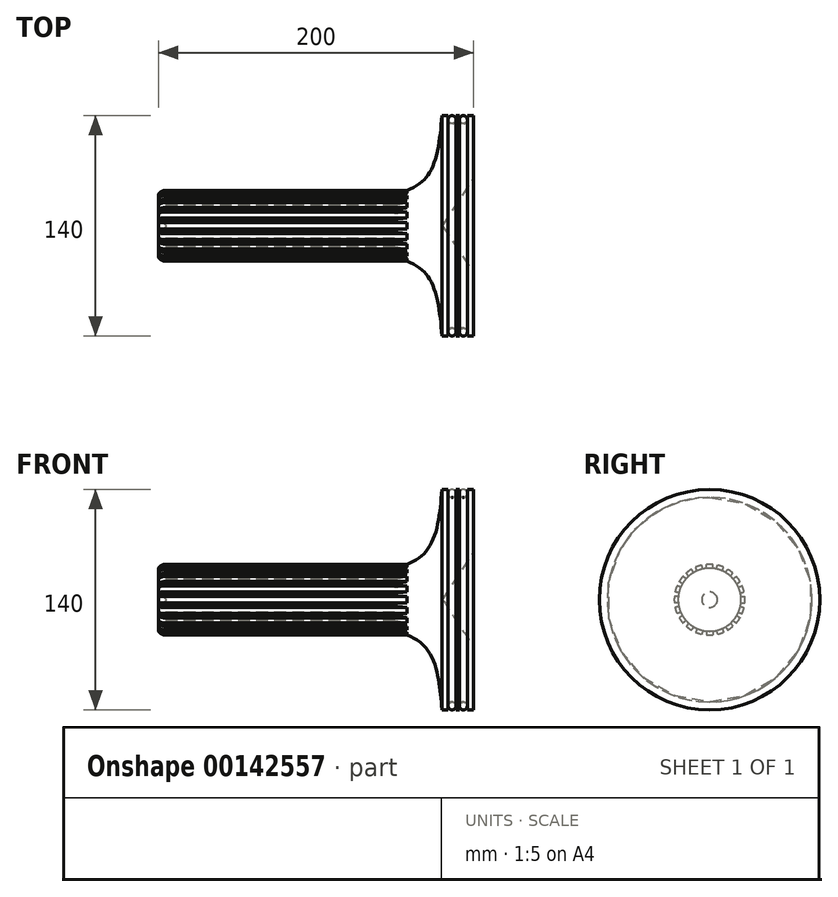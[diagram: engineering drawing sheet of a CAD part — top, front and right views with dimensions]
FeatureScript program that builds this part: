
annotation { "Feature Type Name" : "Feature", "Feature Type Description" : "" }
export const myFeature = defineFeature(function(context is Context, id is Id, definition is map)
    precondition{}
    {
        {
            var Q0;
            Q0=qCreatedBy(makeId("Front.planeOp"),FACE);
            var sketch = newSketch(context, id + "F0", { "sketchPlane" : qUnion([Q0])});
            skLineSegment(sketch, "E0", {"start": v(-143.92, 0) * mm, "end": v(-102.78, 0) * mm, "construction": true});
            skLineSegment(sketch, "E1", {"start": v(-143.92, 4.95) * mm, "end": v(-143.92, 20) * mm});
            skLineSegment(sketch, "E2", {"start": v(-143.92, 20) * mm, "end": v(6.08, 20) * mm});
            skLineSegment(sketch, "E3", {"start": v(56.08, 30) * mm, "end": v(56.08, 70) * mm});
            skFitSpline(sketch, "E4", {"points": [v(6.08, 20) * mm, v(22.5, 27.19) * mm, v(32.06, 42.94) * mm, v(36.08, 70) * mm], "startDerivative": vector(58.15, 17.44) * mm, "endDerivative": vector(6.37, 75.22) * mm});
            skLineSegment(sketch, "E5", {"start": v(-143.92, 4.95) * mm, "end": v(-138.83, 0) * mm});
            skLineSegment(sketch, "E6.trimOffspring", {"start": v(-138.83, 0) * mm, "end": v(36.54, 0) * mm, "construction": true});
            skLineSegment(sketch, "E7", {"start": v(56.08, 30) * mm, "end": v(36.54, 0) * mm});
            skLineSegment(sketch, "E8.trimOffspring", {"start": v(56.08, 0) * mm, "end": v(100.76, 0) * mm, "construction": true});
            skLineSegment(sketch, "E9", {"start": v(36.08, 70) * mm, "end": v(40, 70) * mm});
            skLineSegment(sketch, "E10", {"start": v(40, 70) * mm, "end": v(40, 65) * mm});
            skLineSegment(sketch, "E11", {"start": v(40, 65) * mm, "end": v(45, 65) * mm});
            skLineSegment(sketch, "E12", {"start": v(45, 65) * mm, "end": v(45, 70) * mm});
            skLineSegment(sketch, "E13", {"start": v(45, 70) * mm, "end": v(47.17, 70) * mm});
            skLineSegment(sketch, "E14", {"start": v(47.17, 70) * mm, "end": v(47.17, 65) * mm});
            skLineSegment(sketch, "E15", {"start": v(47.17, 65) * mm, "end": v(52.17, 65) * mm});
            skLineSegment(sketch, "E16", {"start": v(52.17, 65) * mm, "end": v(52.17, 70) * mm});
            skLineSegment(sketch, "E17", {"start": v(52.17, 70) * mm, "end": v(56.08, 70) * mm});
            skLineSegment(sketch, "E18", {"start": v(6.08, 20) * mm, "end": v(6.08, -14.2) * mm, "construction": true});
            skLineSegment(sketch, "E19", {"start": v(6.08, -14.2) * mm, "end": v(6.08, 68.93) * mm, "construction": true});
            skLineSegment(sketch, "E20", {"start": v(-138.83, 0) * mm, "end": v(36.54, 0) * mm});
            skSolve(sketch);
        }
        {
            var Q0;
            Q0=makeQuery(id+"F0.imprint","IMPRINT",FACE,{"disambiguationData":[TD([[makeQuery(id+"F0.imprint","IMPRINT",EDGE,{"derivedFrom":sQuery(id+"F0.wireOp",EDGE,"E1")}),-1.0]])]});
            var sketch = newSketch(context, id + "F1", { "sketchPlane" : qUnion([Q0])});
            skCircle(sketch, "E21", {"center": v(42.5, 67.5) * mm, "radius": 2.5 * mm});
            skCircle(sketch, "E22", {"center": v(49.67, 67.5) * mm, "radius": 2.5 * mm});
            skLineSegment(sketch, "E23.0", {"start": v(40, 65) * mm, "end": v(45, 65) * mm});
            skLineSegment(sketch, "E24.0", {"start": v(47.17, 65) * mm, "end": v(52.17, 65) * mm});
            skSolve(sketch);
        }
        {
            var Q0;
            Q0 = qSketchRegion(id + "F1", true);
            var Q1;
            Q1=sQuery(id+"F0.wireOp",EDGE,"E8.trimOffspring");
            revolve(context, id + "F2", {"entities" : qUnion([Q0]), "axis" : qUnion([Q1]), "revolveType" : RevolveType.FULL});
        }
        {
            var Q0;
            Q0 = qSketchRegion(id + "F0", true);
            var Q1;
            Q1=sQuery(id+"F0.wireOp",EDGE,"E0");
            revolve(context, id + "F3", {"entities" : qUnion([Q0]), "axis" : qUnion([Q1]), "revolveType" : RevolveType.FULL});
        }
        {
            var Q0;
            Q0=makeQuery(id+"F3.opRevolve","SWEPT_FACE",FACE,{"disambiguationData":[OSD([sQuery(id+"F0.wireOp",EDGE,"E1")])]});
            var sketch = newSketch(context, id + "F4", { "sketchPlane" : qUnion([Q0])});
            skPoint(sketch, "E25.middle", {"position": v(0, 0) * mm});
            skPoint(sketch, "E25.right.start.orphan", {"position": v(-6.07, 24.64) * mm});
            skPoint(sketch, "E26.trimOffspring.end.orphan", {"position": v(-6.07, -24.64) * mm});
            skPoint(sketch, "E27.trimOffspring.end.orphan", {"position": v(6.07, -24.64) * mm});
            skPoint(sketch, "E25.left.start.orphan", {"position": v(6.07, 24.64) * mm});
            skLineSegment(sketch, "E28.left", {"start": v(2, 22.41) * mm, "end": v(2, 19.9) * mm});
            skLineSegment(sketch, "E28.right", {"start": v(-2, 22.41) * mm, "end": v(-2, 19.9) * mm});
            skArc(sketch, "E29", {"start": v(2, 19.9) * mm, "mid": v(-20, 0) * mm, "end": v(2, -19.9) * mm});
            skPoint(sketch, "E30.orphan", {"position": v(-2, 29.25) * mm});
            skPoint(sketch, "E31.orphan", {"position": v(2, 29.25) * mm});
            skArc(sketch, "E32.trimOffspring", {"start": v(2, 22.41) * mm, "mid": v(0, 22.5) * mm, "end": v(-2, 22.41) * mm});
            skPoint(sketch, "E33.orphan", {"position": v(-2, -29.25) * mm});
            skPoint(sketch, "E34.orphan", {"position": v(2, -29.25) * mm});
            skSolve(sketch);
        }
        {
            var Q0;
            Q0 = qSketchRegion(id + "F4", true);
            extrude(context, id + "F5", {"entities" : qUnion([Q0]), "endBound" : BoundingType.UP_TO_NEXT, "oppositeDirection" : true, "depth" : 100 * mm});
        }
        {
            var Q0;
            Q0=makeQuery(id+"F5.opExtrude","CAP_EDGE",EDGE,{"disambiguationData":[OSD([sQuery(id+"F4.wireOp",EDGE,"E32.trimOffspring")])],"isStart":true});
            fillet(context, id + "F6", {"entities" : qUnion([Q0]), "radius" : 5 * mm, "tangentPropagation" : true, "allowEdgeOverflow" : false});
        }
        {
            var Q0;
            Q0=makeQuery(id+"F5.opExtrude","SWEPT_BODY",BODY,{"disambiguationData":[OSD([sQuery(id+"F4.wireOp",EDGE,"E28.left"),sQuery(id+"F4.wireOp",EDGE,"E28.right"),sQuery(id+"F4.wireOp",EDGE,"E29"),sQuery(id+"F4.wireOp",EDGE,"E32.trimOffspring")])]});
            var Q1;
            Q1=makeQuery(id+"F3.opRevolve","SWEPT_EDGE",EDGE,{"disambiguationData":[OSD([sQuery(id+"F0.wireOp",EDGE,"E1"),sQuery(id+"F0.wireOp",EDGE,"E2")])]});
            circularPattern(context, id + "F7", {"operationType" : NewBodyOperationType.ADD, "entities" : qUnion([Q0]), "axis" : qUnion([Q1]), "angle" : 360 * degree, "instanceCount" : 20, "equalSpace" : true, "computeTransformsWithoutBuiltin" : true});
        }
        {
            var Q0;
            Q0=makeQuery(id+"F3.opRevolve","SWEPT_EDGE",EDGE,{"disambiguationData":[OSD([sQuery(id+"F0.wireOp",EDGE,"E3"),sQuery(id+"F0.wireOp",EDGE,"E7")])]});
            fillet(context, id + "F8", {"entities" : qUnion([Q0]), "radius" : 5 * mm, "tangentPropagation" : true, "allowEdgeOverflow" : false});
        }
        {
            var Q0;
            Q0=makeQuery(id+"F3.opRevolve","SWEPT_EDGE",EDGE,{"disambiguationData":[OSD([sQuery(id+"F0.wireOp",EDGE,"E10"),sQuery(id+"F0.wireOp",EDGE,"E11")])]});
            var Q1;
            Q1=makeQuery(id+"F3.opRevolve","SWEPT_EDGE",EDGE,{"disambiguationData":[OSD([sQuery(id+"F0.wireOp",EDGE,"E11"),sQuery(id+"F0.wireOp",EDGE,"E12")])]});
            var Q2;
            Q2=makeQuery(id+"F3.opRevolve","SWEPT_EDGE",EDGE,{"disambiguationData":[OSD([sQuery(id+"F0.wireOp",EDGE,"E14"),sQuery(id+"F0.wireOp",EDGE,"E15")])]});
            var Q3;
            Q3=makeQuery(id+"F3.opRevolve","SWEPT_EDGE",EDGE,{"disambiguationData":[OSD([sQuery(id+"F0.wireOp",EDGE,"E15"),sQuery(id+"F0.wireOp",EDGE,"E16")])]});
            fillet(context, id + "F9", {"entities" : qUnion([Q0, Q1, Q2, Q3]), "radius" : 2 * mm, "tangentPropagation" : true, "allowEdgeOverflow" : false});
        }
    });
